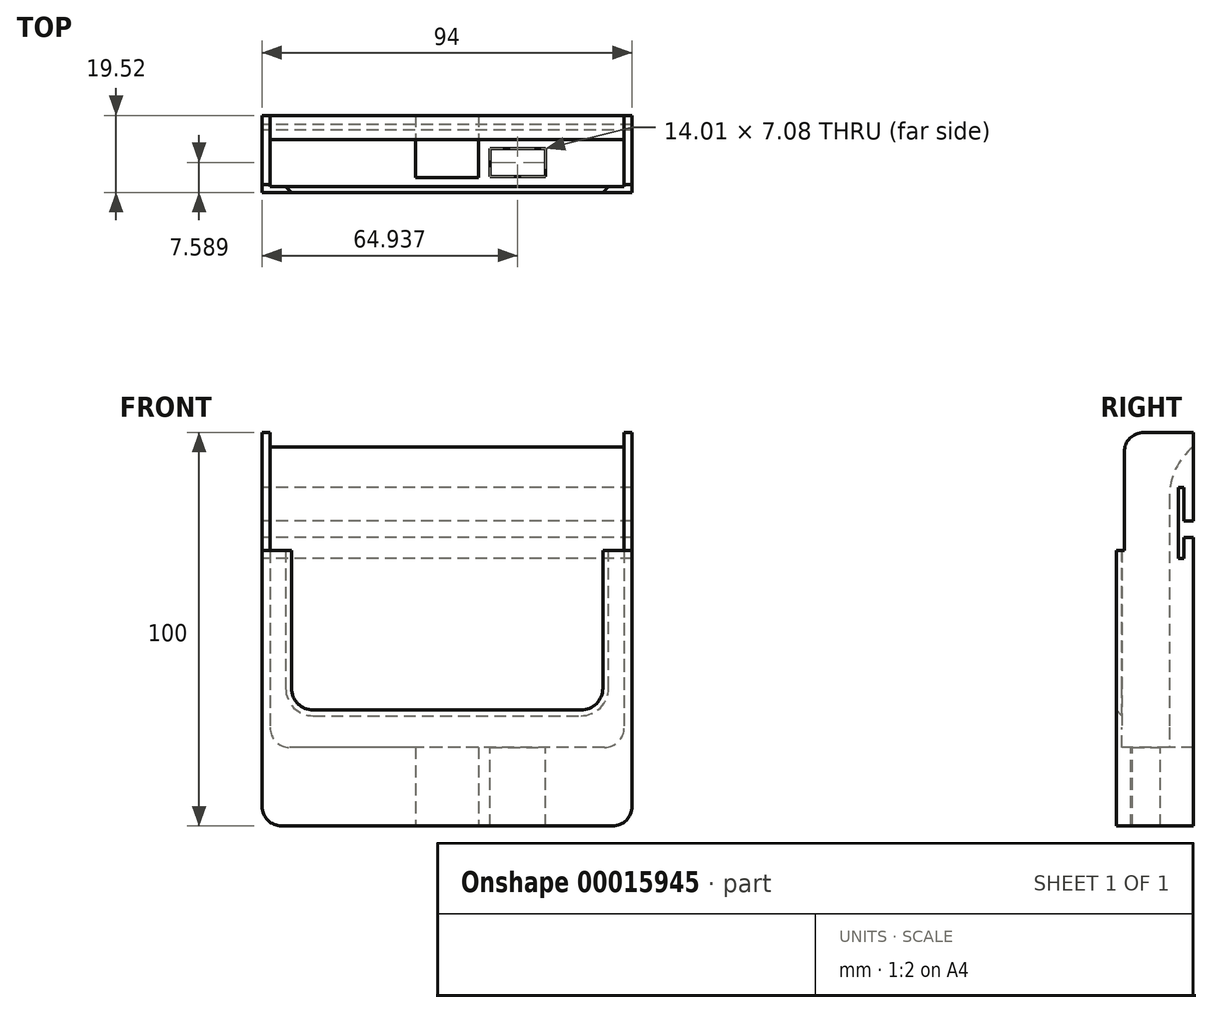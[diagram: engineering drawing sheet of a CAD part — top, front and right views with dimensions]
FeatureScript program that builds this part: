
annotation { "Feature Type Name" : "Feature", "Feature Type Description" : "" }
export const myFeature = defineFeature(function(context is Context, id is Id, definition is map)
    precondition{}
    {
        {
            var Q0;
            Q0=qCreatedBy(makeId("Right.planeOp"),FACE);
            var sketch = newSketch(context, id + "F0", { "sketchPlane" : qUnion([Q0])});
            skLineSegment(sketch, "E0", {"start": v(-13.44, -20) * mm, "end": v(6.08, -20) * mm});
            skLineSegment(sketch, "E1", {"start": v(6.08, -20) * mm, "end": v(6.08, 80) * mm});
            skLineSegment(sketch, "E2", {"start": v(6.08, 80) * mm, "end": v(-11.44, 80) * mm});
            skLineSegment(sketch, "E3", {"start": v(-13.44, 0) * mm, "end": v(-13.44, -20) * mm});
            skLineSegment(sketch, "E4", {"start": v(-13.44, 0) * mm, "end": v(-13.44, 50) * mm});
            skLineSegment(sketch, "E5", {"start": v(-13.44, 50) * mm, "end": v(-11.44, 50) * mm});
            skLineSegment(sketch, "E6", {"start": v(-11.44, 80) * mm, "end": v(-11.44, 50) * mm});
            skLineSegment(sketch, "E7", {"start": v(-13.44, 0) * mm, "end": v(0, 0) * mm, "construction": true});
            skLineSegment(sketch, "E8", {"start": v(4.08, 0) * mm, "end": v(6.08, 0) * mm, "construction": true});
            skLineSegment(sketch, "E9", {"start": v(0, 0) * mm, "end": v(0, 80) * mm, "construction": true});
            skSolve(sketch);
        }
        {
            var Q0;
            Q0=makeQuery(id+"F0.imprint","IMPRINT",FACE,{"disambiguationData":[TD([[makeQuery(id+"F0.imprint","IMPRINT",EDGE,{"derivedFrom":sQuery(id+"F0.wireOp",EDGE,"E0")}),1.0]])]});
            var Q1;
            {var subQ1=sQuery(id+"F0.wireOp",EDGE,"E4");Q1=makeQuery(id+"F0.imprint","IMPRINT",FACE,{"disambiguationData":[TD([[makeQuery(id+"F0.imprint","IMPRINT",EDGE,{"derivedFrom":subQ1}),-1.0]])]});}
            extrude(context, id + "F1", {"entities" : qUnion([Q0, Q1]), "depth" : 92 * mm, "hasSecondDirection" : true, "secondDirectionOppositeDirection" : true, "secondDirectionDepth" : 2 * mm});
        }
        {
            var Q0;
            Q0=qCreatedBy(makeId("Top.planeOp"),FACE);
            var sketch = newSketch(context, id + "F2", { "sketchPlane" : qUnion([Q0])});
            skLineSegment(sketch, "E10.rect.bottom", {"start": v(90, 0) * mm, "end": v(0, 0) * mm});
            skLineSegment(sketch, "E10.rect.top", {"start": v(90, -12) * mm, "end": v(0, -12) * mm});
            skLineSegment(sketch, "E10.rect.left", {"start": v(90, 0) * mm, "end": v(90, -12) * mm});
            skLineSegment(sketch, "E10.rect.right", {"start": v(0, 0) * mm, "end": v(0, -12) * mm});
            skPoint(sketch, "E10.rect.middle", {"position": v(0, 0) * mm});
            skSolve(sketch);
        }
        {
            var Q0;
            Q0=makeQuery(id+"F2.imprint","IMPRINT",FACE,{"disambiguationData":[TD([[makeQuery(id+"F2.imprint","IMPRINT",EDGE,{"derivedFrom":sQuery(id+"F2.wireOp",EDGE,"E10.rect.bottom")}),1.0]])]});
            extrude(context, id + "F3", {"entities" : qUnion([Q0]), "depth" : 156.2 * mm});
        }
        {
            var Q0;
            Q0=makeQuery(id+"F3.opExtrude","SWEPT_BODY",BODY,{"disambiguationData":[OSD([sQuery(id+"F2.wireOp",EDGE,"E10.rect.bottom"),sQuery(id+"F2.wireOp",EDGE,"E10.rect.top"),sQuery(id+"F2.wireOp",EDGE,"E10.rect.left"),sQuery(id+"F2.wireOp",EDGE,"E10.rect.right")])]});
            var Q1;
            Q1=makeQuery(id+"F1.opExtrude","SWEPT_BODY",BODY,{"disambiguationData":[OSD([sQuery(id+"F0.wireOp",EDGE,"E0"),sQuery(id+"F0.wireOp",EDGE,"E1"),sQuery(id+"F0.wireOp",EDGE,"E2"),sQuery(id+"F0.wireOp",EDGE,"E3"),sQuery(id+"F0.wireOp",EDGE,"E4"),sQuery(id+"F0.wireOp",EDGE,"E5"),sQuery(id+"F0.wireOp",EDGE,"E6")])]});
            booleanBodies(context, id + "F4", {"operationType" : BooleanOperationType.SUBTRACTION, "tools" : qUnion([Q0]), "targets" : qUnion([Q1])});
        }
        {
            var Q0;
            Q0=makeQuery(id+"F1.opExtrude","SWEPT_FACE",FACE,{"disambiguationData":[OSD([sQuery(id+"F0.wireOp",EDGE,"E3"),sQuery(id+"F0.wireOp",EDGE,"E4")])]});
            var sketch = newSketch(context, id + "F5", { "sketchPlane" : qUnion([Q0])});
            skPoint(sketch, "E11", {"position": v(0, 50) * mm});
            skPoint(sketch, "E12", {"position": v(90, 50) * mm});
            skLineSegment(sketch, "E13", {"start": v(0, 50) * mm, "end": v(6, 50) * mm, "construction": true});
            skLineSegment(sketch, "E14", {"start": v(90, 50) * mm, "end": v(84, 50) * mm, "construction": true});
            skPoint(sketch, "E15", {"position": v(6, -20) * mm});
            skLineSegment(sketch, "E16", {"start": v(6, -20) * mm, "end": v(6, 10) * mm, "construction": true});
            skPoint(sketch, "E17", {"position": v(84, -20) * mm});
            skLineSegment(sketch, "E18", {"start": v(84, -20) * mm, "end": v(84, 10) * mm, "construction": true});
            skLineSegment(sketch, "E19.bottom", {"start": v(6, 50) * mm, "end": v(84, 50) * mm});
            skLineSegment(sketch, "E19.top", {"start": v(6, 10) * mm, "end": v(84, 10) * mm});
            skLineSegment(sketch, "E19.left", {"start": v(6, 50) * mm, "end": v(6, 10) * mm});
            skLineSegment(sketch, "E19.right", {"start": v(84, 50) * mm, "end": v(84, 10) * mm});
            skLineSegment(sketch, "E20.0", {"start": v(90, 80) * mm, "end": v(90, 50) * mm});
            skLineSegment(sketch, "E20.1", {"start": v(0, 80) * mm, "end": v(0, 50) * mm});
            skSolve(sketch);
        }
        {
            var Q0;
            Q0=qSketchRegion(id+"F5",true);
            extrude(context, id + "F6", {"entities" : qUnion([Q0]), "operationType" : NewBodyOperationType.REMOVE, "oppositeDirection" : true, "depth" : 8 * mm});
        }
        {
            var Q0;
            Q0=makeQuery(id+"F4.opBoolean","COPY",FACE,{"derivedFrom":makeQuery(id+"F3.opExtrude","CAP_FACE",FACE,{"disambiguationData":[OSD([sQuery(id+"F2.wireOp",EDGE,"E10.rect.bottom"),sQuery(id+"F2.wireOp",EDGE,"E10.rect.top"),sQuery(id+"F2.wireOp",EDGE,"E10.rect.left"),sQuery(id+"F2.wireOp",EDGE,"E10.rect.right")])],"isStart":true})});
            var sketch = newSketch(context, id + "F7", { "sketchPlane" : qUnion([Q0])});
            skPoint(sketch, "E21", {"position": v(45, 0) * mm});
            skPoint(sketch, "E22", {"position": v(0, -6) * mm});
            skPoint(sketch, "E23", {"position": v(45, -6) * mm});
            skLineSegment(sketch, "E24.rect.bottom", {"start": v(53, -2.25) * mm, "end": v(37, -2.25) * mm});
            skLineSegment(sketch, "E24.rect.top", {"start": v(53, -9.75) * mm, "end": v(37, -9.75) * mm});
            skLineSegment(sketch, "E24.rect.left", {"start": v(53, -2.25) * mm, "end": v(53, -9.75) * mm});
            skLineSegment(sketch, "E24.rect.right", {"start": v(37, -2.25) * mm, "end": v(37, -9.75) * mm});
            skLineSegment(sketch, "E25.bottom", {"start": v(37, -2.25) * mm, "end": v(53, -2.25) * mm});
            skLineSegment(sketch, "E25.top", {"start": v(37, 13.2) * mm, "end": v(53, 13.2) * mm});
            skLineSegment(sketch, "E25.left", {"start": v(37, -2.25) * mm, "end": v(37, 13.2) * mm});
            skLineSegment(sketch, "E25.right", {"start": v(53, -2.25) * mm, "end": v(53, 13.2) * mm});
            skSolve(sketch);
        }
        {
            var Q0;
            Q0=qSketchRegion(id+"F7",true);
            extrude(context, id + "F8", {"entities" : qUnion([Q0]), "operationType" : NewBodyOperationType.REMOVE, "endBound" : BoundingType.THROUGH_ALL, "oppositeDirection" : true, "depth" : 25 * mm});
        }
        {
            var Q0;
            Q0=makeQuery(id+"F4.opBoolean","COPY",EDGE,{"derivedFrom":makeQuery(id+"F3.opExtrude","CAP_EDGE",EDGE,{"disambiguationData":[OSD([sQuery(id+"F2.wireOp",EDGE,"E10.rect.right")])],"isStart":true})});
            var Q1;
            Q1=makeQuery(id+"F4.opBoolean","COPY",EDGE,{"derivedFrom":makeQuery(id+"F3.opExtrude","CAP_EDGE",EDGE,{"disambiguationData":[OSD([sQuery(id+"F2.wireOp",EDGE,"E10.rect.left")])],"isStart":true})});
            var Q2;
            Q2=makeQuery(id+"F1.opExtrude","CAP_EDGE",EDGE,{"disambiguationData":[OSD([sQuery(id+"F0.wireOp",EDGE,"E0")])],"isStart":true});
            var Q3;
            Q3=makeQuery(id+"F1.opExtrude","CAP_EDGE",EDGE,{"disambiguationData":[OSD([sQuery(id+"F0.wireOp",EDGE,"E0")])],"isStart":false});
            var Q4;
            {var subQ0=sQuery(id+"F0.wireOp",EDGE,"E2");var subQ1=sQuery(id+"F0.wireOp",EDGE,"E6");Q4=makeQuery(id+"F4.opBoolean","SPLIT",EDGE,{"disambiguationData":[TD([makeQuery(id+"F3.opExtrude","SWEPT_FACE",FACE,{"disambiguationData":[OSD([sQuery(id+"F2.wireOp",EDGE,"E10.rect.right")])]})])],"derivedFrom":makeQuery(id+"F1.opExtrude","SWEPT_EDGE",EDGE,{"disambiguationData":[OSD([subQ0,subQ1])]})});}
            var Q5;
            {var subQ0=sQuery(id+"F0.wireOp",EDGE,"E2");var subQ1=sQuery(id+"F0.wireOp",EDGE,"E6");Q5=makeQuery(id+"F4.opBoolean","SPLIT",EDGE,{"disambiguationData":[TD([makeQuery(id+"F3.opExtrude","SWEPT_FACE",FACE,{"disambiguationData":[OSD([sQuery(id+"F2.wireOp",EDGE,"E10.rect.left")])]})])],"derivedFrom":makeQuery(id+"F1.opExtrude","SWEPT_EDGE",EDGE,{"disambiguationData":[OSD([subQ0,subQ1])]})});}
            var Q6;
            Q6=makeQuery(id+"F6.boolean.opBoolean","COPY",EDGE,{"derivedFrom":makeQuery(id+"F6.opExtrude","SWEPT_EDGE",EDGE,{"disambiguationData":[OSD([sQuery(id+"F0.wireOp",EDGE,"E4"),sQuery(id+"F0.wireOp",EDGE,"E5"),sQuery(id+"F5.wireOp",EDGE,"E19.bottom"),sQuery(id+"F5.wireOp",EDGE,"E19.left")])]})});
            var Q7;
            Q7=makeQuery(id+"F6.boolean.opBoolean","COPY",EDGE,{"derivedFrom":makeQuery(id+"F6.opExtrude","SWEPT_EDGE",EDGE,{"disambiguationData":[OSD([sQuery(id+"F0.wireOp",EDGE,"E4"),sQuery(id+"F0.wireOp",EDGE,"E5"),sQuery(id+"F5.wireOp",EDGE,"E19.bottom"),sQuery(id+"F5.wireOp",EDGE,"E19.right")])]})});
            var Q8;
            Q8=makeQuery(id+"F6.boolean.opBoolean","COPY",EDGE,{"derivedFrom":makeQuery(id+"F6.opExtrude","SWEPT_EDGE",EDGE,{"disambiguationData":[OSD([sQuery(id+"F5.wireOp",EDGE,"E19.top"),sQuery(id+"F5.wireOp",EDGE,"E19.left")])]})});
            var Q9;
            Q9=makeQuery(id+"F6.boolean.opBoolean","COPY",EDGE,{"derivedFrom":makeQuery(id+"F6.opExtrude","SWEPT_EDGE",EDGE,{"disambiguationData":[OSD([sQuery(id+"F5.wireOp",EDGE,"E19.top"),sQuery(id+"F5.wireOp",EDGE,"E19.right")])]})});
            fillet(context, id + "F9", {"entities" : qUnion([Q0, Q1, Q2, Q3, Q4, Q5, Q6, Q7, Q8, Q9]), "radius" : 5 * mm, "tangentPropagation" : true, "allowEdgeOverflow" : false});
        }
        {
            var Q0;
            Q0=makeQuery(id+"F6.boolean.opBoolean","INTERSECT",EDGE,{"derivedFrom":[makeQuery(id+"F4.opBoolean","COPY",FACE,{"derivedFrom":makeQuery(id+"F3.opExtrude","SWEPT_FACE",FACE,{"disambiguationData":[OSD([sQuery(id+"F2.wireOp",EDGE,"E10.rect.top")])]})}),makeQuery(id+"F6.opExtrude","SWEPT_FACE",FACE,{"disambiguationData":[OSD([sQuery(id+"F5.wireOp",EDGE,"E19.left")])]})]});
            var Q1;
            Q1=makeQuery(id+"F9.opFillet","BLEND_EDGE",EDGE,{"blendedFrom":[makeQuery(id+"F6.boolean.opBoolean","COPY",EDGE,{"derivedFrom":makeQuery(id+"F6.opExtrude","SWEPT_EDGE",EDGE,{"disambiguationData":[OSD([sQuery(id+"F5.wireOp",EDGE,"E19.top"),sQuery(id+"F5.wireOp",EDGE,"E19.left")])]})}),makeQuery(id+"F4.opBoolean","COPY",FACE,{"derivedFrom":makeQuery(id+"F3.opExtrude","SWEPT_FACE",FACE,{"disambiguationData":[OSD([sQuery(id+"F2.wireOp",EDGE,"E10.rect.top")])]})})],"blendedInto":[makeQuery(id+"F4.opBoolean","COPY",FACE,{"derivedFrom":makeQuery(id+"F3.opExtrude","SWEPT_FACE",FACE,{"disambiguationData":[OSD([sQuery(id+"F2.wireOp",EDGE,"E10.rect.top")])]})})]});
            var Q2;
            Q2=makeQuery(id+"F6.boolean.opBoolean","INTERSECT",EDGE,{"derivedFrom":[makeQuery(id+"F4.opBoolean","COPY",FACE,{"derivedFrom":makeQuery(id+"F3.opExtrude","SWEPT_FACE",FACE,{"disambiguationData":[OSD([sQuery(id+"F2.wireOp",EDGE,"E10.rect.top")])]})}),makeQuery(id+"F6.opExtrude","SWEPT_FACE",FACE,{"disambiguationData":[OSD([sQuery(id+"F5.wireOp",EDGE,"E19.top")])]})]});
            var Q3;
            Q3=makeQuery(id+"F9.opFillet","BLEND_EDGE",EDGE,{"blendedFrom":[makeQuery(id+"F6.boolean.opBoolean","COPY",EDGE,{"derivedFrom":makeQuery(id+"F6.opExtrude","SWEPT_EDGE",EDGE,{"disambiguationData":[OSD([sQuery(id+"F5.wireOp",EDGE,"E19.top"),sQuery(id+"F5.wireOp",EDGE,"E19.right")])]})}),makeQuery(id+"F4.opBoolean","COPY",FACE,{"derivedFrom":makeQuery(id+"F3.opExtrude","SWEPT_FACE",FACE,{"disambiguationData":[OSD([sQuery(id+"F2.wireOp",EDGE,"E10.rect.top")])]})})],"blendedInto":[makeQuery(id+"F4.opBoolean","COPY",FACE,{"derivedFrom":makeQuery(id+"F3.opExtrude","SWEPT_FACE",FACE,{"disambiguationData":[OSD([sQuery(id+"F2.wireOp",EDGE,"E10.rect.top")])]})})]});
            var Q4;
            Q4=makeQuery(id+"F6.boolean.opBoolean","INTERSECT",EDGE,{"derivedFrom":[makeQuery(id+"F4.opBoolean","COPY",FACE,{"derivedFrom":makeQuery(id+"F3.opExtrude","SWEPT_FACE",FACE,{"disambiguationData":[OSD([sQuery(id+"F2.wireOp",EDGE,"E10.rect.top")])]})}),makeQuery(id+"F6.opExtrude","SWEPT_FACE",FACE,{"disambiguationData":[OSD([sQuery(id+"F5.wireOp",EDGE,"E19.right")])]})]});
            var Q5;
            Q5=makeQuery(id+"F9.opFillet","BLEND_EDGE",EDGE,{"blendedFrom":[makeQuery(id+"F6.boolean.opBoolean","COPY",EDGE,{"derivedFrom":makeQuery(id+"F6.opExtrude","SWEPT_EDGE",EDGE,{"disambiguationData":[OSD([sQuery(id+"F0.wireOp",EDGE,"E4"),sQuery(id+"F0.wireOp",EDGE,"E5"),sQuery(id+"F5.wireOp",EDGE,"E19.bottom"),sQuery(id+"F5.wireOp",EDGE,"E19.right")])]})}),makeQuery(id+"F4.opBoolean","COPY",FACE,{"derivedFrom":makeQuery(id+"F3.opExtrude","SWEPT_FACE",FACE,{"disambiguationData":[OSD([sQuery(id+"F2.wireOp",EDGE,"E10.rect.top")])]})})],"blendedInto":[makeQuery(id+"F4.opBoolean","COPY",FACE,{"derivedFrom":makeQuery(id+"F3.opExtrude","SWEPT_FACE",FACE,{"disambiguationData":[OSD([sQuery(id+"F2.wireOp",EDGE,"E10.rect.top")])]})})]});
            var Q6;
            Q6=makeQuery(id+"F9.opFillet","BLEND_EDGE",EDGE,{"blendedFrom":[makeQuery(id+"F6.boolean.opBoolean","COPY",EDGE,{"derivedFrom":makeQuery(id+"F6.opExtrude","SWEPT_EDGE",EDGE,{"disambiguationData":[OSD([sQuery(id+"F0.wireOp",EDGE,"E4"),sQuery(id+"F0.wireOp",EDGE,"E5"),sQuery(id+"F5.wireOp",EDGE,"E19.bottom"),sQuery(id+"F5.wireOp",EDGE,"E19.left")])]})}),makeQuery(id+"F4.opBoolean","COPY",FACE,{"derivedFrom":makeQuery(id+"F3.opExtrude","SWEPT_FACE",FACE,{"disambiguationData":[OSD([sQuery(id+"F2.wireOp",EDGE,"E10.rect.top")])]})})],"blendedInto":[makeQuery(id+"F4.opBoolean","COPY",FACE,{"derivedFrom":makeQuery(id+"F3.opExtrude","SWEPT_FACE",FACE,{"disambiguationData":[OSD([sQuery(id+"F2.wireOp",EDGE,"E10.rect.top")])]})})]});
            chamfer(context, id + "F10", {"entities" : qUnion([Q0, Q1, Q2, Q3, Q4, Q5, Q6]), "width" : 2 * mm, "tangentPropagation" : true});
        }
        {
            var Q0;
            Q0=makeQuery(id+"F4.opBoolean","INTERSECT",EDGE,{"derivedFrom":[makeQuery(id+"F1.opExtrude","SWEPT_FACE",FACE,{"disambiguationData":[OSD([sQuery(id+"F0.wireOp",EDGE,"E2")])]}),makeQuery(id+"F3.opExtrude","SWEPT_FACE",FACE,{"disambiguationData":[OSD([sQuery(id+"F2.wireOp",EDGE,"E10.rect.bottom")])]})]});
            fillet(context, id + "F11", {"entities" : qUnion([Q0]), "radius" : 16.4 * mm, "tangentPropagation" : true, "allowEdgeOverflow" : false});
        }
        {
            var Q0;
            Q0=makeQuery(id+"F4.opBoolean","COPY",FACE,{"derivedFrom":makeQuery(id+"F3.opExtrude","CAP_FACE",FACE,{"disambiguationData":[OSD([sQuery(id+"F2.wireOp",EDGE,"E10.rect.bottom"),sQuery(id+"F2.wireOp",EDGE,"E10.rect.top"),sQuery(id+"F2.wireOp",EDGE,"E10.rect.left"),sQuery(id+"F2.wireOp",EDGE,"E10.rect.right")])],"isStart":true})});
            var sketch = newSketch(context, id + "F12", { "sketchPlane" : qUnion([Q0])});
            skLineSegment(sketch, "E26.bottom", {"start": v(55.93, -9.4) * mm, "end": v(69.94, -9.4) * mm});
            skLineSegment(sketch, "E26.top", {"start": v(55.93, -2.3) * mm, "end": v(69.94, -2.3) * mm});
            skLineSegment(sketch, "E26.left", {"start": v(55.93, -9.4) * mm, "end": v(55.93, -2.3) * mm});
            skLineSegment(sketch, "E26.right", {"start": v(69.94, -9.4) * mm, "end": v(69.94, -2.3) * mm});
            skSolve(sketch);
        }
        {
            var Q0;
            Q0=qSketchRegion(id+"F12",true);
            extrude(context, id + "F13", {"entities" : qUnion([Q0]), "operationType" : NewBodyOperationType.REMOVE, "endBound" : BoundingType.THROUGH_ALL, "oppositeDirection" : true, "depth" : 25 * mm});
        }
        {
            var Q0;
            Q0=makeQuery(id+"F1.opExtrude","CAP_FACE",FACE,{"disambiguationData":[OSD([sQuery(id+"F0.wireOp",EDGE,"E0"),sQuery(id+"F0.wireOp",EDGE,"E1"),sQuery(id+"F0.wireOp",EDGE,"E2"),sQuery(id+"F0.wireOp",EDGE,"E3"),sQuery(id+"F0.wireOp",EDGE,"E4"),sQuery(id+"F0.wireOp",EDGE,"E5"),sQuery(id+"F0.wireOp",EDGE,"E6")])],"isStart":true});
            var sketch = newSketch(context, id + "F14", { "sketchPlane" : qUnion([Q0])});
            skLineSegment(sketch, "E27.bottom", {"start": v(-6.08, 57.47) * mm, "end": v(-3.74, 57.47) * mm});
            skLineSegment(sketch, "E27.top", {"start": v(-6.08, 53.3) * mm, "end": v(-3.74, 53.3) * mm});
            skLineSegment(sketch, "E27.left", {"start": v(-6.08, 57.47) * mm, "end": v(-6.08, 53.3) * mm});
            skLineSegment(sketch, "E27.right", {"start": v(-3.74, 57.47) * mm, "end": v(-3.74, 53.3) * mm});
            skLineSegment(sketch, "E28.bottom", {"start": v(-3.74, 65.96) * mm, "end": v(-2.34, 65.96) * mm});
            skLineSegment(sketch, "E28.top", {"start": v(-3.74, 47.99) * mm, "end": v(-2.34, 47.99) * mm});
            skLineSegment(sketch, "E28.left", {"start": v(-3.74, 65.96) * mm, "end": v(-3.74, 47.99) * mm});
            skLineSegment(sketch, "E28.right", {"start": v(-2.34, 65.96) * mm, "end": v(-2.34, 47.99) * mm});
            skSolve(sketch);
        }
        {
            var Q0;
            {var subQ3=sQuery(id+"F14.wireOp",EDGE,"E28.bottom");Q0=makeQuery(id+"F14.imprint","IMPRINT",FACE,{"disambiguationData":[TD([[makeQuery(id+"F14.imprint","IMPRINT",EDGE,{"derivedFrom":subQ3}),-1.0]])]});}
            var Q1;
            {var subQ0=sQuery(id+"F14.wireOp",EDGE,"E27.bottom");Q1=makeQuery(id+"F14.imprint","IMPRINT",FACE,{"disambiguationData":[TD([[makeQuery(id+"F14.imprint","IMPRINT",EDGE,{"derivedFrom":subQ0}),-1.0]])]});}
            extrude(context, id + "F15", {"entities" : qUnion([Q0, Q1]), "operationType" : NewBodyOperationType.REMOVE, "endBound" : BoundingType.THROUGH_ALL, "oppositeDirection" : true, "depth" : 25 * mm});
        }
    });
